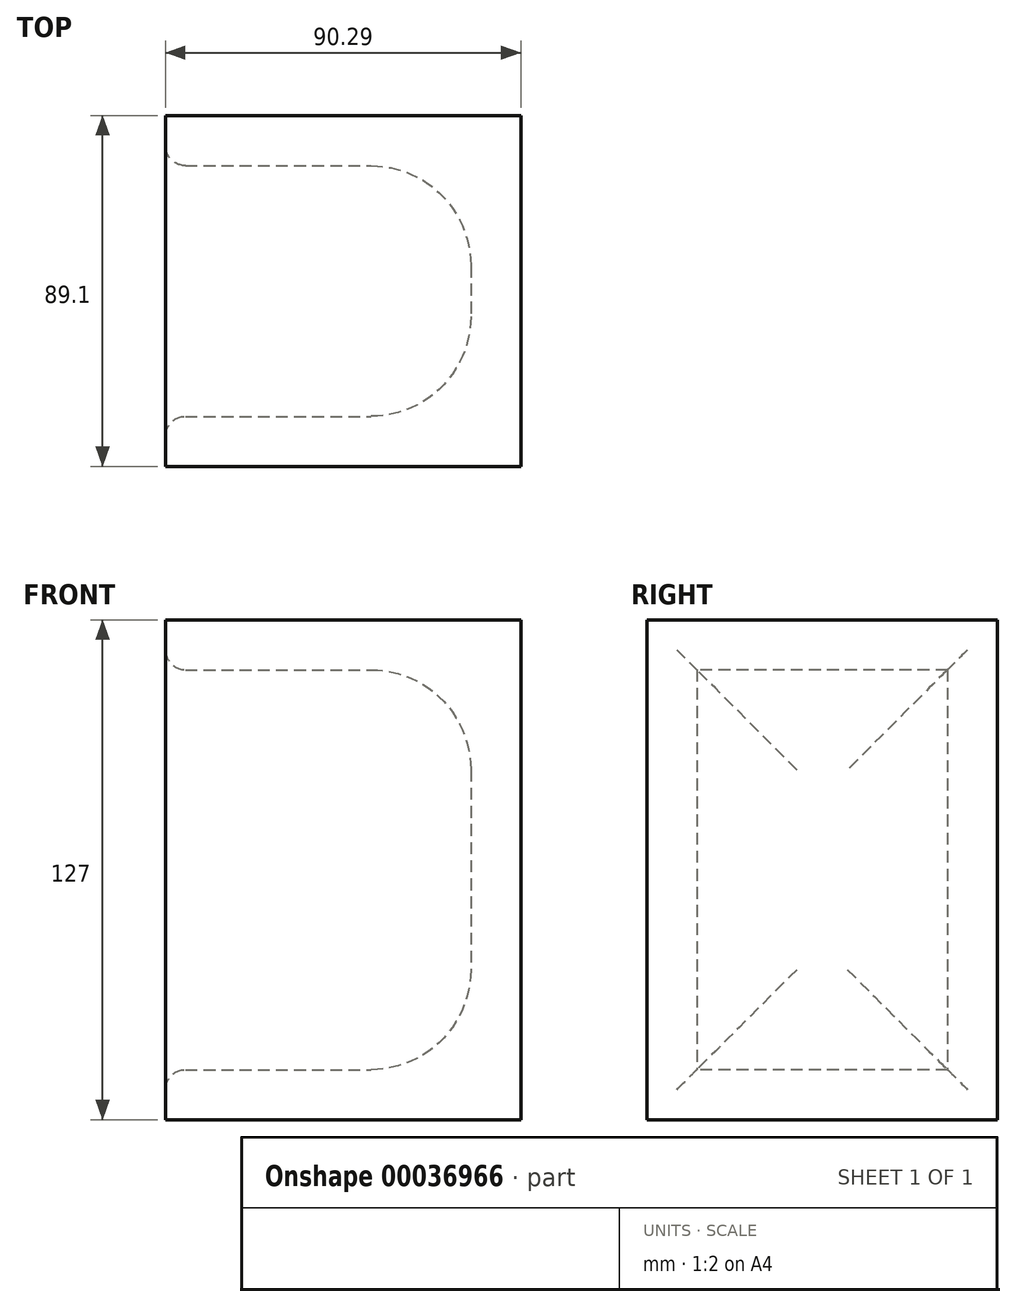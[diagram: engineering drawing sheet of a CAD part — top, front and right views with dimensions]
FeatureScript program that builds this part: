
annotation { "Feature Type Name" : "Feature", "Feature Type Description" : "" }
export const myFeature = defineFeature(function(context is Context, id is Id, definition is map)
    precondition{}
    {
        {
            var Q0;
            Q0=qCreatedBy(makeId("Top.planeOp"),FACE);
            var sketch = newSketch(context, id + "F0", { "sketchPlane" : qUnion([Q0])});
            skLineSegment(sketch, "E0.bottom", {"start": v(-44.4, 46.64) * mm, "end": v(45.9, 46.64) * mm});
            skLineSegment(sketch, "E0.top", {"start": v(-44.4, -42.46) * mm, "end": v(45.9, -42.46) * mm});
            skLineSegment(sketch, "E0.left", {"start": v(-44.4, 46.64) * mm, "end": v(-44.4, -42.46) * mm});
            skLineSegment(sketch, "E0.right", {"start": v(45.9, 46.64) * mm, "end": v(45.9, -42.46) * mm});
            skSolve(sketch);
        }
        {
            var Q0;
            Q0=makeQuery(id+"F0.imprint","IMPRINT",FACE,{"disambiguationData":[TD([[makeQuery(id+"F0.imprint","IMPRINT",EDGE,{"derivedFrom":sQuery(id+"F0.wireOp",EDGE,"E0.bottom")}),-1.0]])]});
            extrude(context, id + "F1", {"entities" : qUnion([Q0]), "depth" : 127 * mm});
        }
        {
            var Q0;
            Q0=makeQuery(id+"F1.opExtrude","SWEPT_FACE",FACE,{"disambiguationData":[OSD([sQuery(id+"F0.wireOp",EDGE,"E0.left")])]});
            shell(context, id + "F2", {"entities" : qUnion([Q0]), "thickness" : 12.7 * mm});
        }
        {
            var Q0;
            Q0=makeQuery(id+"F2.opShell","OFFSET_EDGE",EDGE,{"disambiguationData":[OSD([sQuery(id+"F0.wireOp",EDGE,"E0.top"),sQuery(id+"F0.wireOp",EDGE,"E0.left")])]});
            var Q1;
            {var subQ0=sQuery(id+"F0.wireOp",EDGE,"E0.left");Q1=makeQuery(id+"F2.opShell","OFFSET_EDGE",EDGE,{"disambiguationData":[OSD([subQ0]),TDD([makeQuery(id+"F1.opExtrude","CAP_EDGE",EDGE,{"disambiguationData":[OSD([subQ0])],"isStart":true})])]});}
            var Q2;
            Q2=makeQuery(id+"F2.opShell","OFFSET_EDGE",EDGE,{"disambiguationData":[OSD([sQuery(id+"F0.wireOp",EDGE,"E0.bottom"),sQuery(id+"F0.wireOp",EDGE,"E0.left")])]});
            var Q3;
            {var subQ0=sQuery(id+"F0.wireOp",EDGE,"E0.left");Q3=makeQuery(id+"F2.opShell","OFFSET_EDGE",EDGE,{"disambiguationData":[OSD([subQ0]),TDD([makeQuery(id+"F1.opExtrude","CAP_EDGE",EDGE,{"disambiguationData":[OSD([subQ0])],"isStart":false})])]});}
            fillet(context, id + "F3", {"entities" : qUnion([Q0, Q1, Q2, Q3]), "radius" : 5.08 * mm, "tangentPropagation" : true, "allowEdgeOverflow" : false});
        }
        {
            var Q0;
            {var subQ0=sQuery(id+"F0.wireOp",EDGE,"E0.right");Q0=makeQuery(id+"F2.opShell","OFFSET_EDGE",EDGE,{"disambiguationData":[OSD([subQ0]),TDD([makeQuery(id+"F1.opExtrude","CAP_EDGE",EDGE,{"disambiguationData":[OSD([subQ0])],"isStart":true})])]});}
            var Q1;
            Q1=makeQuery(id+"F2.opShell","OFFSET_EDGE",EDGE,{"disambiguationData":[OSD([sQuery(id+"F0.wireOp",EDGE,"E0.bottom"),sQuery(id+"F0.wireOp",EDGE,"E0.right")])]});
            var Q2;
            {var subQ0=sQuery(id+"F0.wireOp",EDGE,"E0.right");Q2=makeQuery(id+"F2.opShell","OFFSET_EDGE",EDGE,{"disambiguationData":[OSD([subQ0]),TDD([makeQuery(id+"F1.opExtrude","CAP_EDGE",EDGE,{"disambiguationData":[OSD([subQ0])],"isStart":false})])]});}
            var Q3;
            Q3=makeQuery(id+"F2.opShell","OFFSET_EDGE",EDGE,{"disambiguationData":[OSD([sQuery(id+"F0.wireOp",EDGE,"E0.top"),sQuery(id+"F0.wireOp",EDGE,"E0.right")])]});
            fillet(context, id + "F4", {"entities" : qUnion([Q0, Q1, Q2, Q3]), "radius" : 25.4 * mm, "tangentPropagation" : true, "allowEdgeOverflow" : false});
        }
    });
